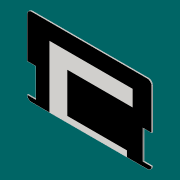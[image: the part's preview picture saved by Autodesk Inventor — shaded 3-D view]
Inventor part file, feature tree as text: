
AUTODESK INVENTOR PART (.ipt)
format: ipt  version: 2016 (Build 200138000, 138)  size: 207,360 bytes
history: native  units: mm
features: sketch x5, other x4, extrude x3, projected_geometry x3, fillet x1, mirror x1
ambient origin geometry x8: Origin, YZ Plane, XZ Plane, XY Plane, X Axis, Y Axis, Z Axis, Center Point
bodies: Solid1 (feature_tree)
feature tree (17):
  extrude  "Extrusion1"  Depth=53.98mm
  fillet  "Fillet1"  Radius=0.76mm
  extrude  "Extrusion2"  Depth=2.88mm
  extrude  "Extrusion3"  Depth=5.588mm
  mirror  "Mirror1"
  other  "Decal1"
  other  "Decal2"
  sketch  "Sketch1"  dims[d0=85.6mm d1=53.98mm d2=0.76mm]
  sketch  "Sketch2"  dims[d3=0.0mm d4=2.88mm]
  projected_geometry  "Projected Loop1"
  sketch  "Sketch3"  dims[d5=5.588mm d6=5.588mm]
  sketch  "Sketch4"  dims[d7=3.0mm]
  projected_geometry  "Projected Loop2"
  sketch  "Sketch5"  dims[d8=3.0mm d9=20.0mm d10=20.0mm d11=0.76mm d12=0.0mm d13=3.0mm d14=3.0mm d15=0.76mm d16=1.5mm d17=1.5mm d18=1.5mm d19=0.76mm d20=0.0mm]
  projected_geometry  "Projected Loop3"
  other  "Image8"
  other  "Image9"
